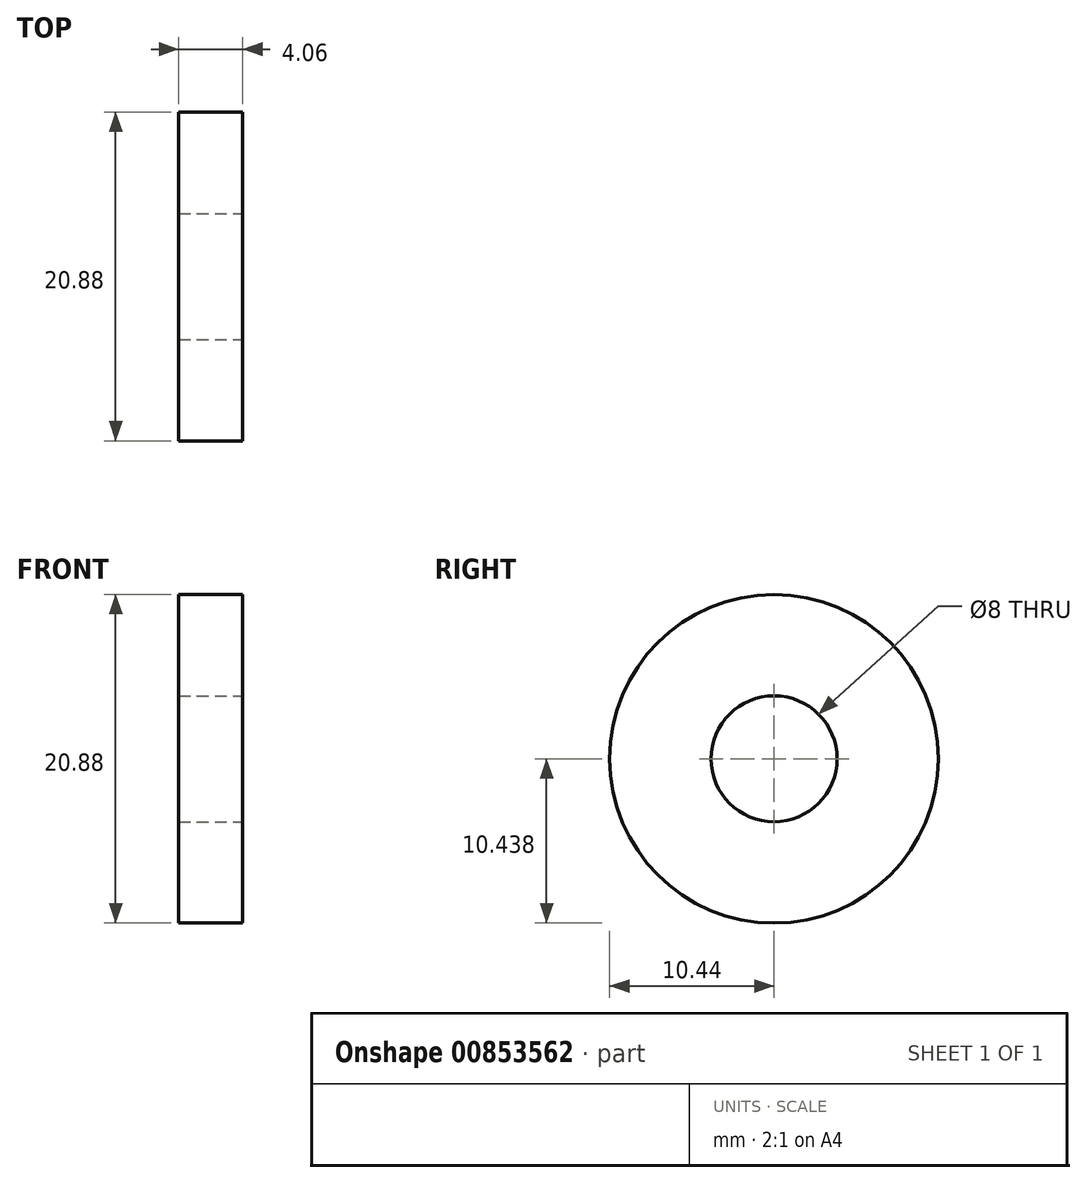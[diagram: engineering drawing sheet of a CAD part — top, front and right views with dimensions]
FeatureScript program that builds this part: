
annotation { "Feature Type Name" : "Feature", "Feature Type Description" : "" }
export const myFeature = defineFeature(function(context is Context, id is Id, definition is map)
    precondition{}
    {
        {
            var Q0;
            Q0=qCreatedBy(makeId("Right.planeOp"),FACE);
            var sketch = newSketch(context, id + "F0", { "sketchPlane" : qUnion([Q0])});
            skCircle(sketch, "E0", {"center": v(0, -1.55) * mm, "radius": 10.44 * mm});
            skSolve(sketch);
        }
        {
            var Q0;
            Q0 = qSketchRegion(id + "F0", true);
            extrude(context, id + "F1", {"entities" : qUnion([Q0]), "oppositeDirection" : true, "depth" : 4.06 * mm, "offsetDistance" : 25.4 * mm});
        }
        {
            var Q0;
            Q0=makeQuery(id+"F1.opExtrude","CAP_FACE",FACE,{"disambiguationData":[OSD([sQuery(id+"F0.wireOp",EDGE,"E0")])],"isStart":true});
            var sketch = newSketch(context, id + "F2", { "sketchPlane" : qUnion([Q0])});
            skPoint(sketch, "E1", {"position": v(0, -1.55) * mm});
            skSolve(sketch);
        }
        {
            var Q0;
            Q0=sQuery(id+"F2.wireOp",VERTEX,"E1");
            var Q1;
            Q1=makeQuery(id+"F1.opExtrude","SWEPT_BODY",BODY,{"disambiguationData":[OSD([sQuery(id+"F0.wireOp",EDGE,"E0")])]});
            hole(context, id + "F3", {"style" : HoleStyle.SIMPLE, "endStyle" : HoleEndStyle.THROUGH, "holeDiameter" : 8 * mm, "majorDiameter" : 9.52 * mm, "isTappedThrough" : true, "tappedDepth" : 12.7 * mm, "tapClearance" : 3, "locations" : qUnion([Q0]), "scope" : qUnion([Q1])});
        }
    });
